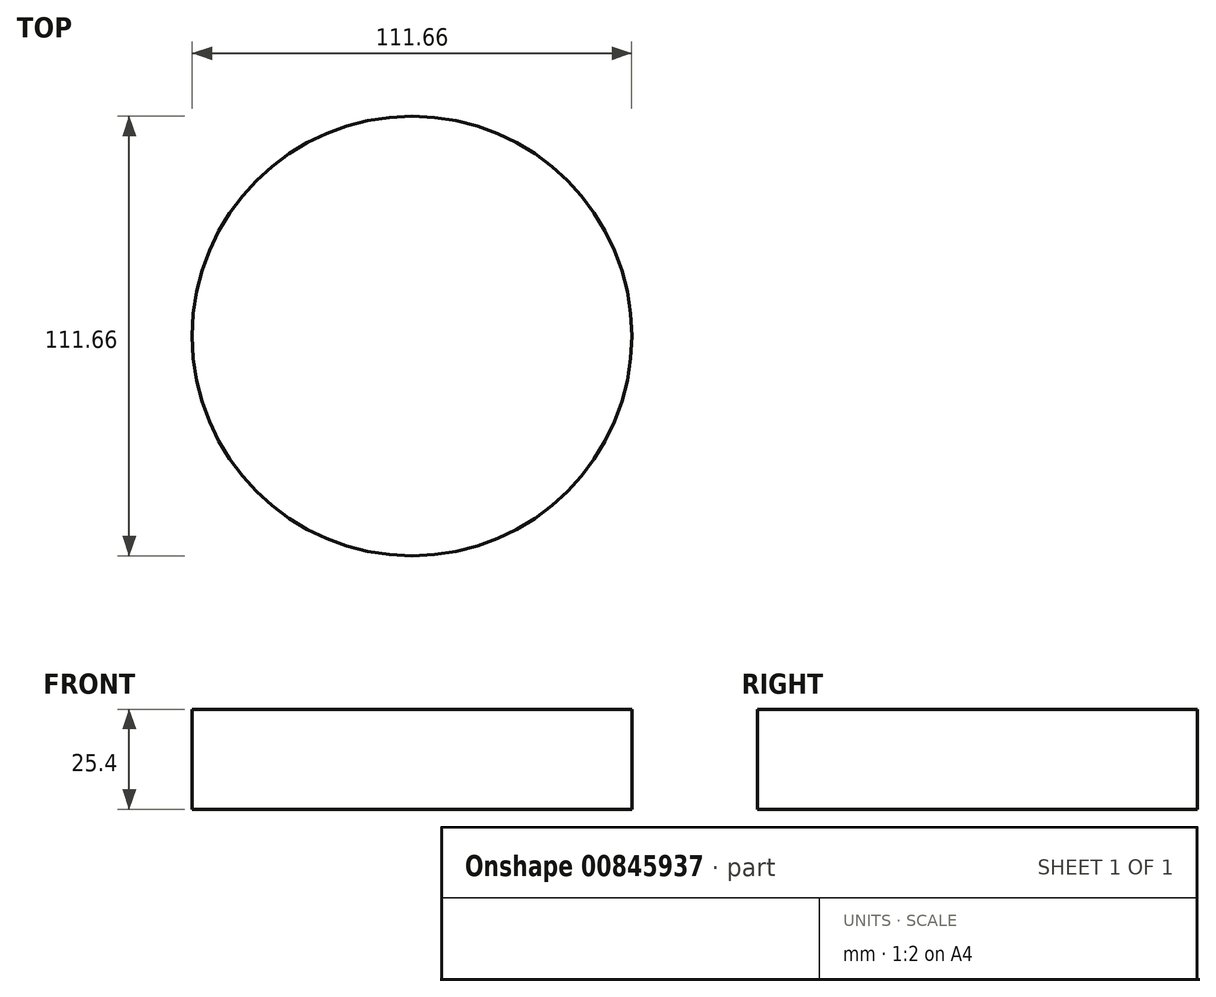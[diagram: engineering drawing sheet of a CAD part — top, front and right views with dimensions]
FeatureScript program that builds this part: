
annotation { "Feature Type Name" : "Feature", "Feature Type Description" : "" }
export const myFeature = defineFeature(function(context is Context, id is Id, definition is map)
    precondition{}
    {
        {
            var Q0;
            Q0=qCreatedBy(makeId("Top.planeOp"),FACE);
            var sketch = newSketch(context, id + "F0", { "sketchPlane" : qUnion([Q0])});
            skCircle(sketch, "E0", {"center": v(0, 0) * mm, "radius": 55.83 * mm});
            skSolve(sketch);
        }
        {
            var Q0;
            Q0=makeQuery(id+"F0.imprint","IMPRINT",FACE,{"disambiguationData":[TD([[makeQuery(id+"F0.imprint","IMPRINT",EDGE,{"derivedFrom":sQuery(id+"F0.wireOp",EDGE,"E0")}),1.0]])]});
            extrude(context, id + "F1", {"entities" : qUnion([Q0]), "depth" : 25.4 * mm, "offsetDistance" : 25.4 * mm});
        }
    });
